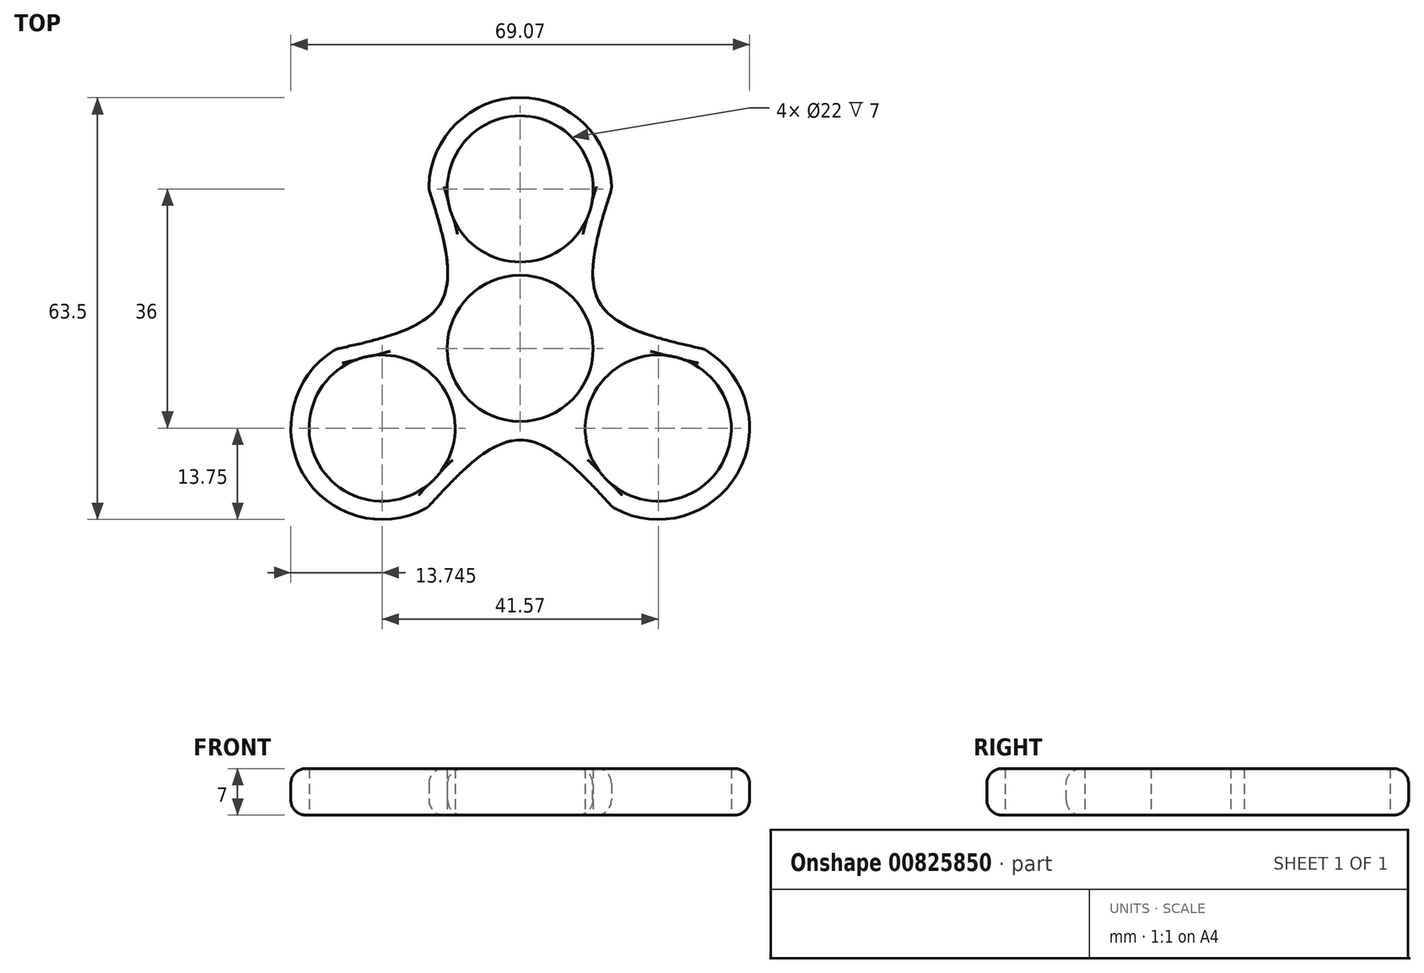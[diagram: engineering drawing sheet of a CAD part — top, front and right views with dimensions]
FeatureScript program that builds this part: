
annotation { "Feature Type Name" : "Feature", "Feature Type Description" : "" }
export const myFeature = defineFeature(function(context is Context, id is Id, definition is map)
    precondition{}
    {
        {
            var Q0;
            Q0=qCreatedBy(makeId("Top.planeOp"),FACE);
            var sketch = newSketch(context, id + "F0", { "sketchPlane" : qUnion([Q0])});
            skCircle(sketch, "E0", {"center": v(0, 0) * mm, "radius": 11 * mm});
            skPoint(sketch, "E1.top.end.orphan", {"position": v(-31.84, 27.57) * mm});
            skPoint(sketch, "E2.orphan", {"position": v(31.84, 27.58) * mm});
            skPoint(sketch, "E1.bottom.end.orphan", {"position": v(-31.84, -27.58) * mm});
            skPoint(sketch, "E1.bottom.start.orphan", {"position": v(31.84, -27.57) * mm});
            skCircle(sketch, "E3", {"center": v(0, 24) * mm, "radius": 11 * mm});
            skCircle(sketch, "E4", {"center": v(20.79, -12) * mm, "radius": 11 * mm});
            skCircle(sketch, "E5", {"center": v(-20.78, -12) * mm, "radius": 11 * mm});
            skArc(sketch, "E6.0", {"start": v(11.64, 16.68) * mm, "mid": v(0, 37.75) * mm, "end": v(-11.64, 16.68) * mm});
            skArc(sketch, "E7.0", {"start": v(8.62, -18.42) * mm, "mid": v(32.7, -18.87) * mm, "end": v(20.26, 1.74) * mm});
            skArc(sketch, "E8.0", {"start": v(-20.26, 1.74) * mm, "mid": v(-32.7, -18.87) * mm, "end": v(-8.62, -18.41) * mm});
            skFitSpline(sketch, "E9", {"points": [v(-13.75, 24) * mm, v(-11.94, 6.9) * mm, v(-27.66, -0.1) * mm], "startDerivative": vector(12.39, -39.28) * mm, "endDerivative": vector(-40.2, -8.9) * mm});
            skFitSpline(sketch, "E10", {"points": [v(-13.9, -23.9) * mm, v(0, -13.79) * mm, v(13.91, -23.9) * mm], "startDerivative": vector(27.82, 30.37) * mm, "endDerivative": vector(27.82, -30.36) * mm});
            skFitSpline(sketch, "E11", {"points": [v(27.66, -0.1) * mm, v(11.94, 6.9) * mm, v(13.75, 24) * mm], "startDerivative": vector(-40.2, 8.9) * mm, "endDerivative": vector(12.38, 39.27) * mm});
            skSolve(sketch);
        }
        {
            var Q0;
            Q0=makeQuery(id+"F0.imprint","IMPRINT",FACE,{"disambiguationData":[TD([[makeQuery(id+"F0.imprint","IMPRINT",EDGE,{"derivedFrom":sQuery(id+"F0.wireOp",EDGE,"E0")}),-1.0]])]});
            extrude(context, id + "F1", {"entities" : qUnion([Q0]), "depth" : 7 * mm, "offsetDistance" : 25 * mm});
        }
        {
            var Q0;
            Q0=makeQuery(id+"F1.opExtrude","SWEPT_FACE",FACE,{"disambiguationData":[OSD([sQuery(id+"F0.wireOp",EDGE,"E6.0")])]});
            var Q1;
            Q1=makeQuery(id+"F1.opExtrude","SWEPT_FACE",FACE,{"disambiguationData":[OSD([sQuery(id+"F0.wireOp",EDGE,"E11")])]});
            var Q2;
            Q2=makeQuery(id+"F1.opExtrude","SWEPT_FACE",FACE,{"disambiguationData":[OSD([sQuery(id+"F0.wireOp",EDGE,"E7.0")])]});
            var Q3;
            Q3=makeQuery(id+"F1.opExtrude","SWEPT_FACE",FACE,{"disambiguationData":[OSD([sQuery(id+"F0.wireOp",EDGE,"E10")])]});
            var Q4;
            Q4=makeQuery(id+"F1.opExtrude","SWEPT_FACE",FACE,{"disambiguationData":[OSD([sQuery(id+"F0.wireOp",EDGE,"E8.0")])]});
            var Q5;
            Q5=makeQuery(id+"F1.opExtrude","SWEPT_FACE",FACE,{"disambiguationData":[OSD([sQuery(id+"F0.wireOp",EDGE,"E9")])]});
            fillet(context, id + "F2", {"entities" : qUnion([Q0, Q1, Q2, Q3, Q4, Q5]), "radius" : 2.25 * mm, "tangentPropagation" : true, "allowEdgeOverflow" : false});
        }
    });
